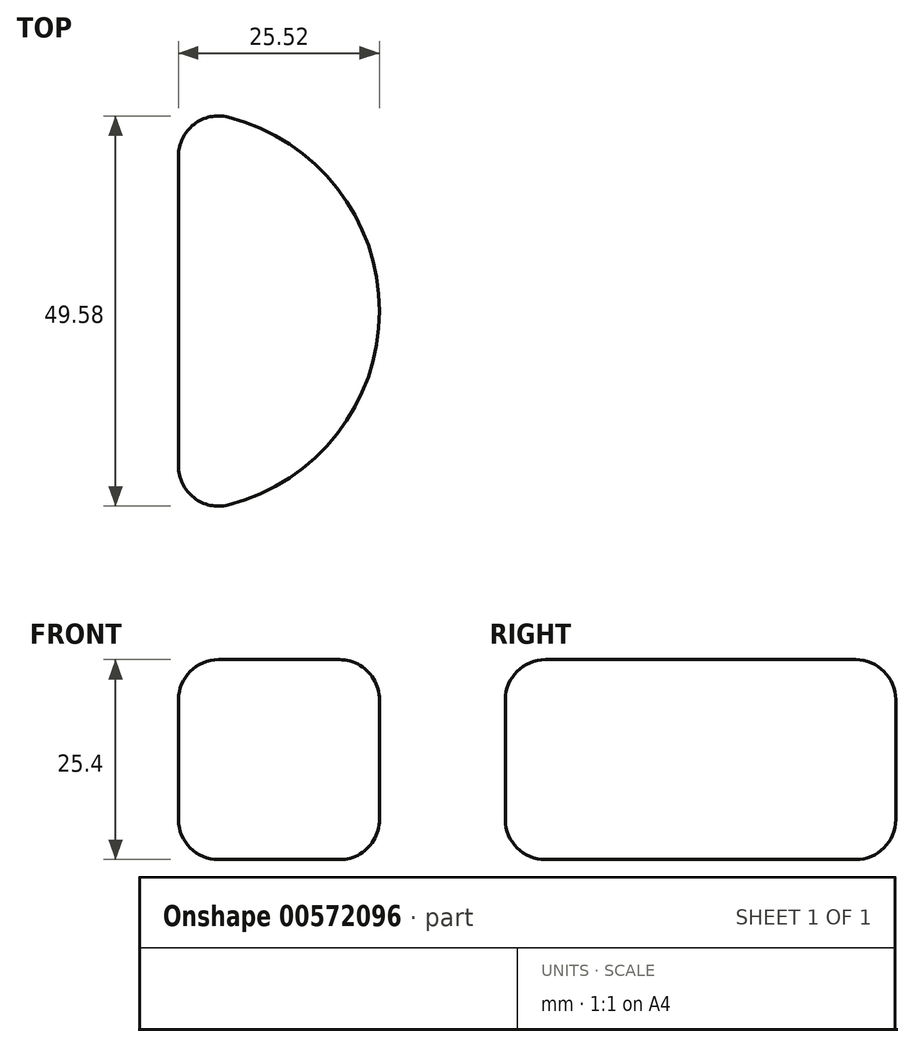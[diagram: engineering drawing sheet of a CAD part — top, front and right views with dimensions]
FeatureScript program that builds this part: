
annotation { "Feature Type Name" : "Feature", "Feature Type Description" : "" }
export const myFeature = defineFeature(function(context is Context, id is Id, definition is map)
    precondition{}
    {
        {
            var Q0;
            Q0=qCreatedBy(makeId("Top.planeOp"),FACE);
            var sketch = newSketch(context, id + "F0", { "sketchPlane" : qUnion([Q0])});
            skArc(sketch, "E0", {"start": v(0, 16.94) * mm, "mid": v(25.52, 42.34) * mm, "end": v(0, 67.74) * mm});
            skLineSegment(sketch, "E1", {"start": v(0, 67.74) * mm, "end": v(0, 16.94) * mm});
            skSolve(sketch);
        }
        {
            var Q0;
            Q0=makeQuery(id+"F0.imprint","IMPRINT",FACE,{"disambiguationData":[TD([[makeQuery(id+"F0.imprint","IMPRINT",EDGE,{"derivedFrom":sQuery(id+"F0.wireOp",EDGE,"E0")}),1.0]])]});
            extrude(context, id + "F1", {"entities" : qUnion([Q0]), "depth" : 25.4 * mm, "offsetDistance" : 25.4 * mm});
        }
        {
            var Q0;
            Q0=makeQuery(id+"F1.opExtrude","CAP_FACE",FACE,{"disambiguationData":[OSD([sQuery(id+"F0.wireOp",EDGE,"E0"),sQuery(id+"F0.wireOp",EDGE,"E1")])],"isStart":false});
            var Q1;
            Q1=makeQuery(id+"F1.opExtrude","CAP_FACE",FACE,{"disambiguationData":[OSD([sQuery(id+"F0.wireOp",EDGE,"E0"),sQuery(id+"F0.wireOp",EDGE,"E1")])],"isStart":true});
            var Q2;
            Q2=makeQuery(id+"F1.opExtrude","SWEPT_FACE",FACE,{"disambiguationData":[OSD([sQuery(id+"F0.wireOp",EDGE,"E0")])]});
            fillet(context, id + "F2", {"entities" : qUnion([Q0, Q1, Q2]), "radius" : 5.08 * mm, "tangentPropagation" : true, "allowEdgeOverflow" : false});
        }
    });
